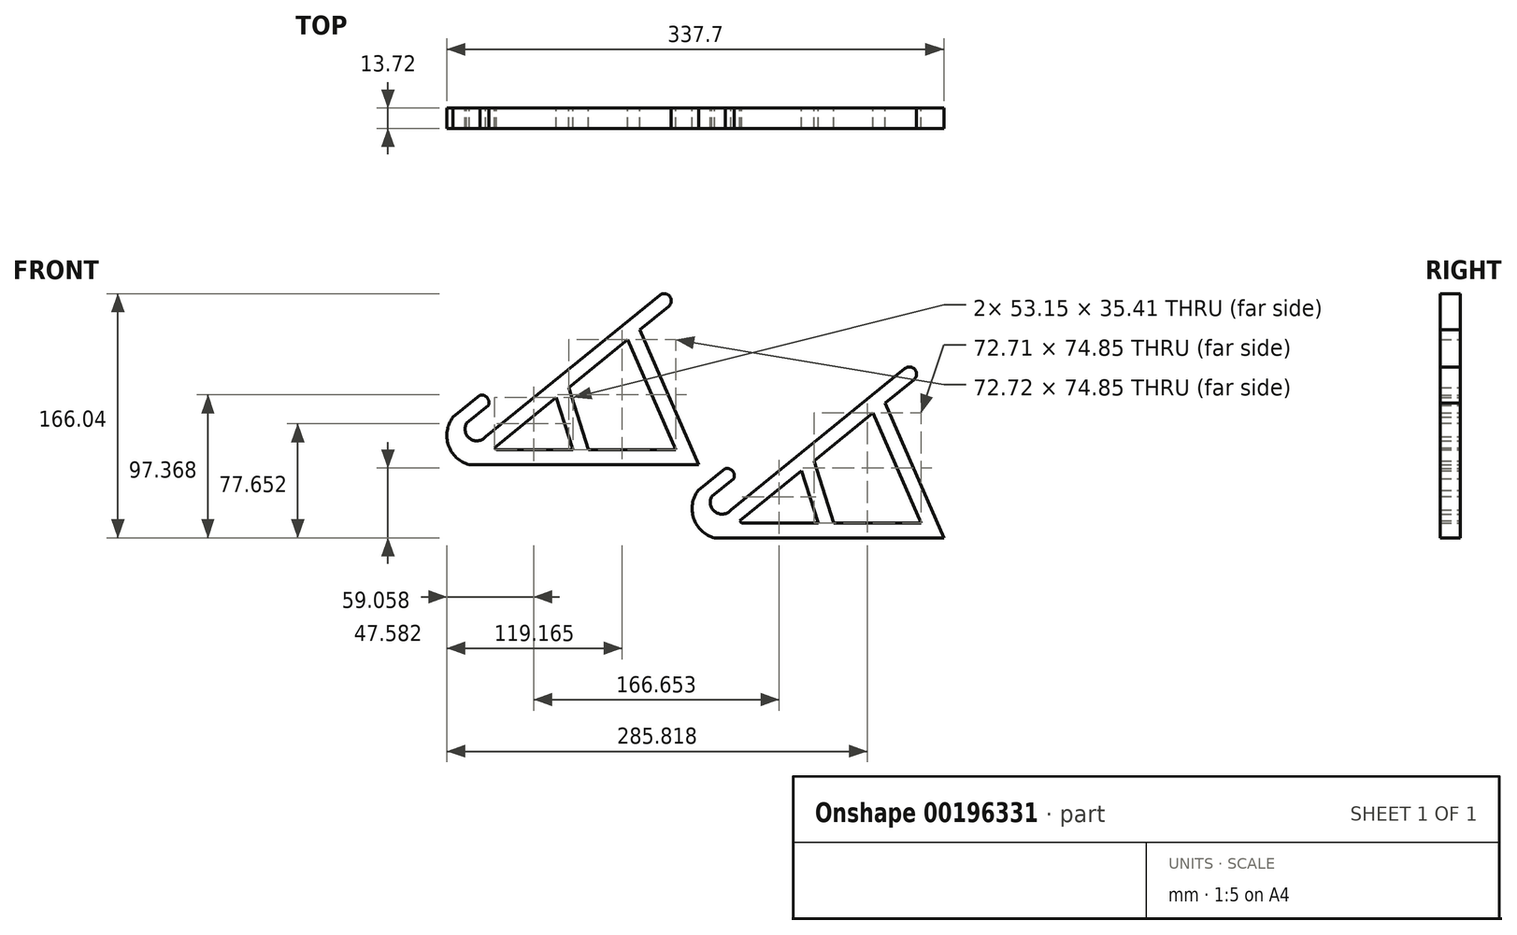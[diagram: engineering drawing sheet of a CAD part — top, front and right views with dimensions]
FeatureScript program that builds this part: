
annotation { "Feature Type Name" : "Feature", "Feature Type Description" : "" }
export const myFeature = defineFeature(function(context is Context, id is Id, definition is map)
    precondition{}
    {
        {
            var Q0;
            Q0=qCreatedBy(makeId("Front.planeOp"),FACE);
            var sketch = newSketch(context, id + "F0", { "sketchPlane" : qUnion([Q0])});
            skLineSegment(sketch, "E0", {"start": v(-39.32, -9.08) * mm, "end": v(59.22, 71.04) * mm});
            skLineSegment(sketch, "E1", {"start": v(59.22, 71.04) * mm, "end": v(65.31, 63.55) * mm});
            skLineSegment(sketch, "E2", {"start": v(65.31, 63.55) * mm, "end": v(-33.23, -16.57) * mm});
            skLineSegment(sketch, "E3", {"start": v(-33.23, -16.57) * mm, "end": v(-39.32, -9.08) * mm});
            skLineSegment(sketch, "E4", {"start": v(-44.24, -28.1) * mm, "end": v(105.34, -28.1) * mm});
            skLineSegment(sketch, "E5", {"start": v(-33.23, -16.57) * mm, "end": v(-32.1, -17.94) * mm});
            skLineSegment(sketch, "E6", {"start": v(-32.1, -17.94) * mm, "end": v(89.81, -17.94) * mm});
            skLineSegment(sketch, "E7", {"start": v(65.31, 63.55) * mm, "end": v(105.34, -28.1) * mm});
            skLineSegment(sketch, "E8", {"start": v(89.81, -17.94) * mm, "end": v(57.13, 56.9) * mm});
            skLineSegment(sketch, "E9", {"start": v(59.22, 71.04) * mm, "end": v(78.93, 87.07) * mm});
            skLineSegment(sketch, "E10", {"start": v(65.31, 63.55) * mm, "end": v(85.02, 79.58) * mm});
            skLineSegment(sketch, "E11", {"start": v(-52.31, 0) * mm, "end": v(-48.93, 2.75) * mm});
            skLineSegment(sketch, "E12", {"start": v(-50.6, 13.17) * mm, "end": v(-43.18, 19.21) * mm});
            skLineSegment(sketch, "E13", {"start": v(-52.31, 0) * mm, "end": v(-37.41, 12.12) * mm});
            skArc(sketch, "E14", {"start": v(-37.41, 12.12) * mm, "mid": v(-38.2, 17.36) * mm, "end": v(-43.18, 19.21) * mm});
            skLineSegment(sketch, "E15", {"start": v(-44.24, -28.1) * mm, "end": v(-50.52, -28.1) * mm});
            skArc(sketch, "E16", {"start": v(-52.31, 0) * mm, "mid": v(-49.96, -10.47) * mm, "end": v(-39.32, -9.08) * mm});
            skArc(sketch, "E17", {"start": v(-61.6, 4.23) * mm, "mid": v(-64.59, -14.86) * mm, "end": v(-50.52, -28.1) * mm});
            skLineSegment(sketch, "E18", {"start": v(-61.6, 4.23) * mm, "end": v(-50.6, 13.17) * mm});
            skLineSegment(sketch, "E19", {"start": v(19.93, -17.94) * mm, "end": v(8.63, 17.47) * mm});
            skLineSegment(sketch, "E20", {"start": v(30.59, -17.94) * mm, "end": v(17.1, 24.35) * mm});
            skArc(sketch, "E21", {"start": v(85.02, 79.58) * mm, "mid": v(85.72, 86.37) * mm, "end": v(78.93, 87.07) * mm});
            skLineSegment(sketch, "E22", {"start": v(127.34, -58.86) * mm, "end": v(225.87, 21.26) * mm});
            skLineSegment(sketch, "E23", {"start": v(225.87, 21.26) * mm, "end": v(231.96, 13.77) * mm});
            skLineSegment(sketch, "E24", {"start": v(231.96, 13.77) * mm, "end": v(133.42, -66.35) * mm});
            skLineSegment(sketch, "E25", {"start": v(133.42, -66.35) * mm, "end": v(127.34, -58.86) * mm});
            skLineSegment(sketch, "E26", {"start": v(122.41, -77.9) * mm, "end": v(271.99, -77.9) * mm});
            skLineSegment(sketch, "E27", {"start": v(133.42, -66.35) * mm, "end": v(134.55, -67.73) * mm});
            skLineSegment(sketch, "E28", {"start": v(134.55, -67.73) * mm, "end": v(256.47, -67.73) * mm});
            skLineSegment(sketch, "E29", {"start": v(231.96, 13.77) * mm, "end": v(271.99, -77.9) * mm});
            skLineSegment(sketch, "E30", {"start": v(256.47, -67.73) * mm, "end": v(223.78, 7.12) * mm});
            skLineSegment(sketch, "E31", {"start": v(225.87, 21.26) * mm, "end": v(245.58, 37.28) * mm});
            skLineSegment(sketch, "E32", {"start": v(231.96, 13.77) * mm, "end": v(251.67, 29.8) * mm});
            skLineSegment(sketch, "E33", {"start": v(114.34, -49.79) * mm, "end": v(117.72, -47.04) * mm});
            skLineSegment(sketch, "E34", {"start": v(116.04, -36.62) * mm, "end": v(123.47, -30.58) * mm});
            skLineSegment(sketch, "E35", {"start": v(114.34, -49.79) * mm, "end": v(129.24, -37.67) * mm});
            skArc(sketch, "E36", {"start": v(129.24, -37.67) * mm, "mid": v(128.45, -32.43) * mm, "end": v(123.47, -30.58) * mm});
            skLineSegment(sketch, "E37", {"start": v(122.41, -77.9) * mm, "end": v(116.13, -77.9) * mm});
            skArc(sketch, "E38", {"start": v(114.34, -49.79) * mm, "mid": v(116.7, -60.25) * mm, "end": v(127.34, -58.86) * mm});
            skArc(sketch, "E39", {"start": v(105.05, -45.55) * mm, "mid": v(102.07, -64.64) * mm, "end": v(116.13, -77.9) * mm});
            skLineSegment(sketch, "E40", {"start": v(105.05, -45.55) * mm, "end": v(116.04, -36.62) * mm});
            skLineSegment(sketch, "E41", {"start": v(186.58, -67.73) * mm, "end": v(175.28, -32.32) * mm});
            skLineSegment(sketch, "E42", {"start": v(197.24, -67.73) * mm, "end": v(183.75, -25.43) * mm});
            skArc(sketch, "E43", {"start": v(251.67, 29.8) * mm, "mid": v(252.37, 36.58) * mm, "end": v(245.58, 37.28) * mm});
            skSolve(sketch);
        }
        {
            var Q0;
            Q0=makeQuery(id+"F0.imprint","IMPRINT",FACE,{"disambiguationData":[TD([[makeQuery(id+"F0.imprint","IMPRINT",EDGE,{"derivedFrom":sQuery(id+"F0.wireOp",EDGE,"E3")}),1.0]])]});
            extrude(context, id + "F1", {"entities" : qUnion([Q0]), "depth" : 13.72 * mm});
        }
        {
            var Q0;
            Q0=makeQuery(id+"F0.imprint","IMPRINT",FACE,{"disambiguationData":[TD([[makeQuery(id+"F0.imprint","IMPRINT",EDGE,{"derivedFrom":sQuery(id+"F0.wireOp",EDGE,"E0")}),-1.0]])]});
            var Q1;
            Q1=makeQuery(id+"F0.imprint","IMPRINT",FACE,{"disambiguationData":[TD([[makeQuery(id+"F0.imprint","IMPRINT",EDGE,{"derivedFrom":sQuery(id+"F0.wireOp",EDGE,"E1")}),1.0]])]});
            extrude(context, id + "F2", {"entities" : qUnion([Q0, Q1]), "operationType" : NewBodyOperationType.ADD, "depth" : 13.72 * mm});
        }
        {
            var Q0;
            {var subQ0=sQuery(id+"F0.wireOp",EDGE,"E19");Q0=makeQuery(id+"F0.imprint","IMPRINT",FACE,{"disambiguationData":[TD([[makeQuery(id+"F0.imprint","IMPRINT",EDGE,{"derivedFrom":subQ0}),-1.0]])]});}
            extrude(context, id + "F3", {"entities" : qUnion([Q0]), "operationType" : NewBodyOperationType.ADD, "depth" : 13.72 * mm});
        }
        {
            var Q0;
            Q0=makeQuery(id+"F0.imprint","IMPRINT",FACE,{"disambiguationData":[TD([[makeQuery(id+"F0.imprint","IMPRINT",EDGE,{"derivedFrom":sQuery(id+"F0.wireOp",EDGE,"E25")}),1.0]])]});
            var Q1;
            Q1=makeQuery(id+"F0.imprint","IMPRINT",FACE,{"disambiguationData":[TD([[makeQuery(id+"F0.imprint","IMPRINT",EDGE,{"derivedFrom":sQuery(id+"F0.wireOp",EDGE,"E22")}),-1.0]])]});
            var Q2;
            {var subQ0=sQuery(id+"F0.wireOp",EDGE,"E41");Q2=makeQuery(id+"F0.imprint","IMPRINT",FACE,{"disambiguationData":[TD([[makeQuery(id+"F0.imprint","IMPRINT",EDGE,{"derivedFrom":subQ0}),-1.0]])]});}
            var Q3;
            Q3=makeQuery(id+"F0.imprint","IMPRINT",FACE,{"disambiguationData":[TD([[makeQuery(id+"F0.imprint","IMPRINT",EDGE,{"derivedFrom":sQuery(id+"F0.wireOp",EDGE,"E23")}),1.0]])]});
            extrude(context, id + "F4", {"entities" : qUnion([Q0, Q1, Q2, Q3]), "depth" : 13.72 * mm});
        }
    });
